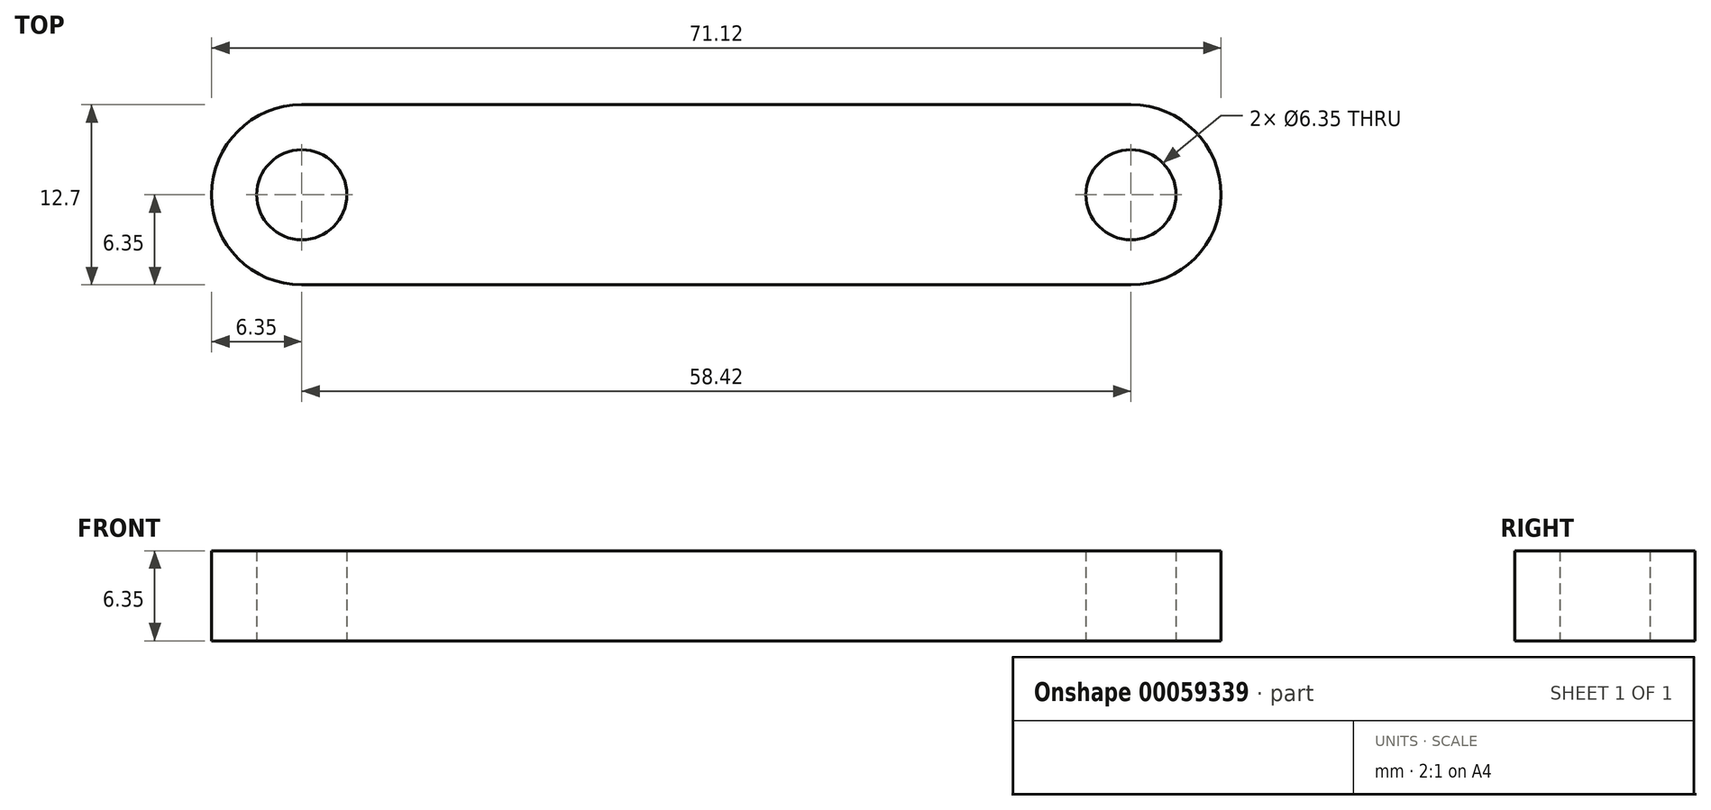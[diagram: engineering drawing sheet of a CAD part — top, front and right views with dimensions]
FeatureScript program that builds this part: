
annotation { "Feature Type Name" : "Feature", "Feature Type Description" : "" }
export const myFeature = defineFeature(function(context is Context, id is Id, definition is map)
    precondition{}
    {
        {
            var Q0;
            Q0=qCreatedBy(makeId("Top.planeOp"),FACE);
            var sketch = newSketch(context, id + "F0", { "sketchPlane" : qUnion([Q0])});
            skLineSegment(sketch, "E0.bottom", {"start": v(-29.21, 6.35) * mm, "end": v(29.21, 6.35) * mm});
            skLineSegment(sketch, "E0.top", {"start": v(-29.21, -6.35) * mm, "end": v(29.21, -6.35) * mm});
            skArc(sketch, "E1", {"start": v(-29.21, 6.35) * mm, "mid": v(-35.56, 0) * mm, "end": v(-29.21, -6.35) * mm});
            skArc(sketch, "E2", {"start": v(29.21, -6.35) * mm, "mid": v(35.56, 0) * mm, "end": v(29.21, 6.35) * mm});
            skCircle(sketch, "E3", {"center": v(-29.21, 0) * mm, "radius": 3.18 * mm});
            skCircle(sketch, "E4", {"center": v(29.21, 0) * mm, "radius": 3.18 * mm});
            skSolve(sketch);
        }
        {
            var Q0;
            Q0=makeQuery(id+"F0.imprint","IMPRINT",FACE,{"disambiguationData":[TD([[makeQuery(id+"F0.imprint","IMPRINT",EDGE,{"derivedFrom":sQuery(id+"F0.wireOp",EDGE,"E0.bottom")}),-1.0]])]});
            extrude(context, id + "F1", {"entities" : qUnion([Q0]), "depth" : 6.35 * mm});
        }
    });
